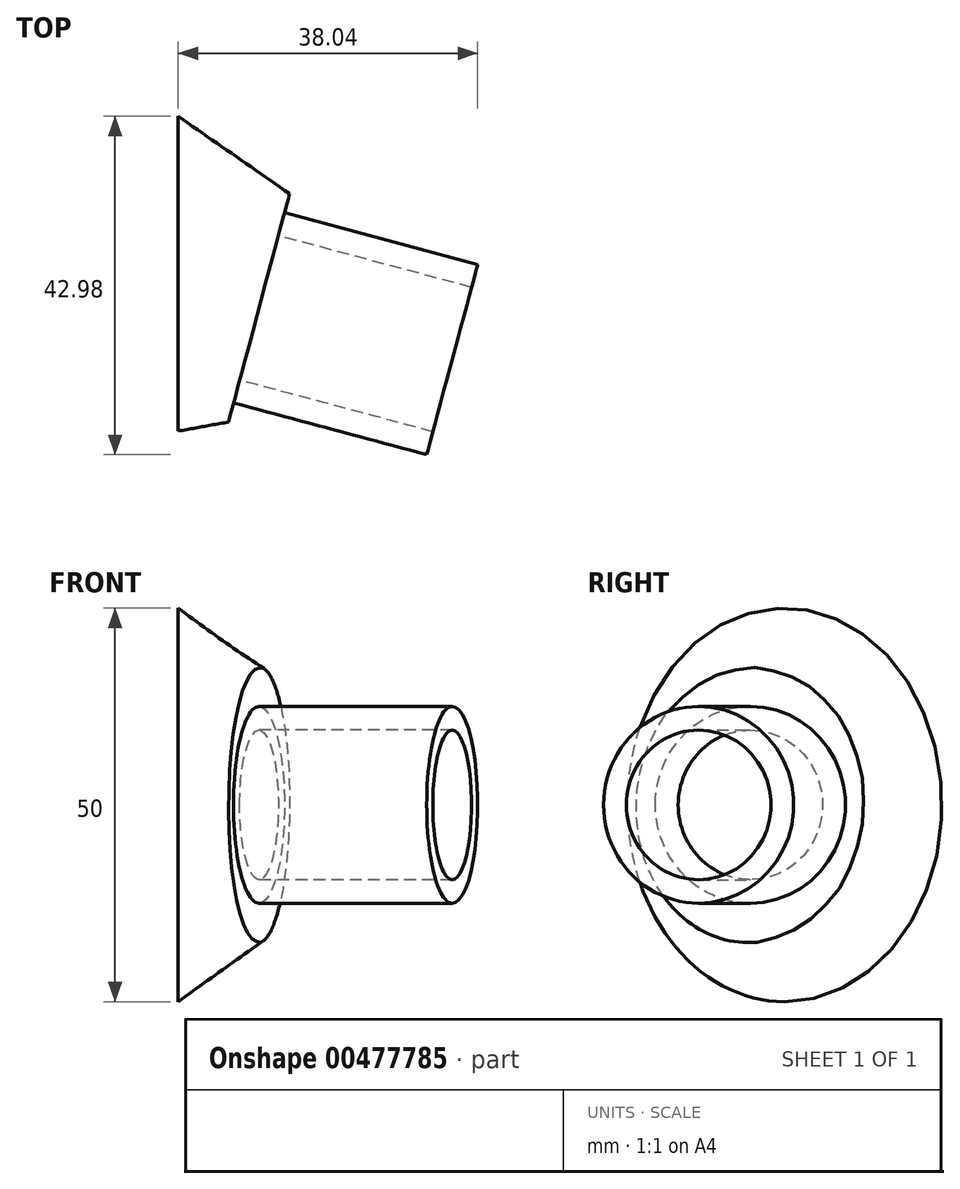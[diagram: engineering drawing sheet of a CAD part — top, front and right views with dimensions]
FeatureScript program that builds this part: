
annotation { "Feature Type Name" : "Feature", "Feature Type Description" : "" }
export const myFeature = defineFeature(function(context is Context, id is Id, definition is map)
    precondition{}
    {
        {
            var Q0;
            Q0=qCreatedBy(makeId("Front.planeOp"),FACE);
            var sketch = newSketch(context, id + "F0", { "sketchPlane" : qUnion([Q0])});
            skLineSegment(sketch, "E0", {"start": v(10.17, 22.95) * mm, "end": v(10.17, -24.03) * mm});
            skSolve(sketch);
        }
        {
            var Q0;
            Q0=sQuery(id+"F0.wireOp",EDGE,"E0");
            cPlane(context, id + "F1", {"entities" : qUnion([Q0]), "cplaneType" : CPlaneType.LINE_ANGLE, "offset" : 25 * mm, "angle" : 15 * degree, "width" : 150 * mm, "height" : 150 * mm});
        }
        {
            var Q0;
            Q0=qCreatedBy(id+"F1.planeOp",FACE);
            var sketch = newSketch(context, id + "F2", { "sketchPlane" : qUnion([Q0])});
            skEllipse(sketch, "E1", {"center": v(-3, 0) * mm, "majorRadius": 17.5 * mm, "minorRadius": 15 * mm, "majorAxis": v(-0.07, 1)});
            skSolve(sketch);
        }
        {
            var Q0;
            Q0=qCreatedBy(id+"F1.planeOp",FACE);
            var sketch = newSketch(context, id + "F3", { "sketchPlane" : qUnion([Q0])});
            skCircle(sketch, "E2", {"center": v(-3, 0) * mm, "radius": 12.5 * mm});
            skSolve(sketch);
        }
        {
            var Q0;
            Q0 = qSketchRegion(id + "F3", true);
            extrude(context, id + "F4", {"entities" : qUnion([Q0]), "oppositeDirection" : true, "depth" : 25.4 * mm, "offsetDistance" : 25 * mm});
        }
        {
            var Q0;
            Q0=qCreatedBy(makeId("Right.planeOp"),FACE);
            var sketch = newSketch(context, id + "F5", { "sketchPlane" : qUnion([Q0])});
            skEllipse(sketch, "E3", {"center": v(4.7, 0) * mm, "majorRadius": 25 * mm, "minorRadius": 20 * mm, "majorAxis": v(0, -1)});
            skSolve(sketch);
        }
        {
            var Q1;
            Q1=makeQuery(id+"F5.imprint","IMPRINT",FACE,{"disambiguationData":[TD([[makeQuery(id+"F5.imprint","IMPRINT",EDGE,{"derivedFrom":sQuery(id+"F5.wireOp",EDGE,"E3")}),1.0]])]});
            var Q2;
            Q2=makeQuery(id+"F2.imprint","IMPRINT",FACE,{"disambiguationData":[TD([[makeQuery(id+"F2.imprint","IMPRINT",EDGE,{"derivedFrom":sQuery(id+"F2.wireOp",EDGE,"E1")}),1.0]])]});
            loft(context, id + "F6", {"operationType" : NewBodyOperationType.ADD, "sheetProfilesArray" : [{ "sheetProfileEntities" : qUnion([Q1]) }, { "sheetProfileEntities" : qUnion([Q2]) }]});
        }
        {
            var Q0;
            Q0=sQuery(id+"F3.wireOp",VERTEX,"E2.center");
            var Q1;
            Q1=makeQuery(id+"F4.opExtrude","SWEPT_BODY",BODY,{"disambiguationData":[OSD([sQuery(id+"F3.wireOp",EDGE,"E2")])]});
            hole(context, id + "F7", {"style" : HoleStyle.SIMPLE, "endStyle" : HoleEndStyle.THROUGH, "holeDiameter" : 19 * mm, "isTappedThrough" : true, "tappedDepth" : 12 * mm, "tapClearance" : 3, "locations" : qUnion([Q0]), "scope" : qUnion([Q1])});
        }
    });
